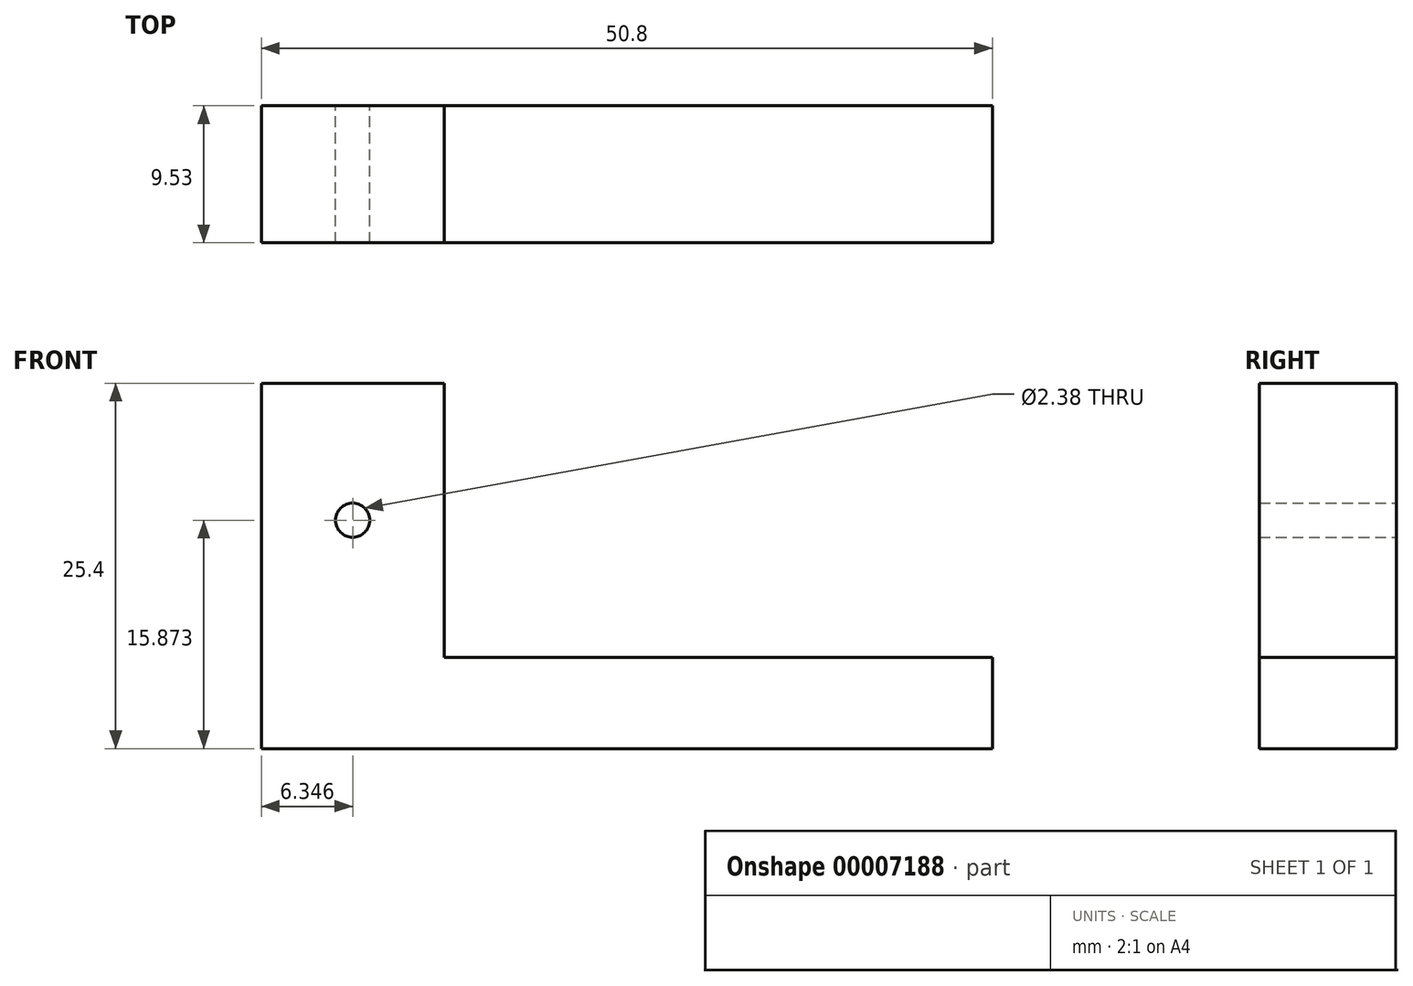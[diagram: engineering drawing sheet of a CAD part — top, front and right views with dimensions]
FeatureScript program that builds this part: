
annotation { "Feature Type Name" : "Feature", "Feature Type Description" : "" }
export const myFeature = defineFeature(function(context is Context, id is Id, definition is map)
    precondition{}
    {
        {
            var Q0;
            Q0=qCreatedBy(makeId("Front.planeOp"),FACE);
            var sketch = newSketch(context, id + "F0", { "sketchPlane" : qUnion([Q0])});
            skLineSegment(sketch, "E0", {"start": v(-18.26, 20.95) * mm, "end": v(-18.26, -4.45) * mm});
            skLineSegment(sketch, "E1", {"start": v(-18.26, -4.45) * mm, "end": v(32.54, -4.45) * mm});
            skLineSegment(sketch, "E2", {"start": v(32.54, -4.45) * mm, "end": v(32.54, 1.9) * mm});
            skLineSegment(sketch, "E3", {"start": v(32.54, 1.9) * mm, "end": v(-5.56, 1.9) * mm});
            skLineSegment(sketch, "E4", {"start": v(-5.56, 1.9) * mm, "end": v(-5.56, 20.95) * mm});
            skLineSegment(sketch, "E5", {"start": v(-5.56, 20.95) * mm, "end": v(-18.26, 20.95) * mm});
            skCircle(sketch, "E6", {"center": v(-11.91, 11.42) * mm, "radius": 1.2 * mm});
            skSolve(sketch);
        }
        {
            var Q0;
            Q0=makeQuery(id+"F0.imprint","IMPRINT",FACE,{"disambiguationData":[TD([[makeQuery(id+"F0.imprint","IMPRINT",EDGE,{"derivedFrom":sQuery(id+"F0.wireOp",EDGE,"E0")}),1.0]])]});
            extrude(context, id + "F1", {"entities" : qUnion([Q0]), "depth" : 9.52 * mm});
        }
    });
